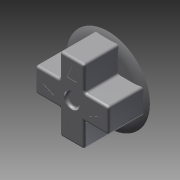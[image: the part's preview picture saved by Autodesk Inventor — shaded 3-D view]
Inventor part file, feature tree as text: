
AUTODESK INVENTOR PART (.ipt)
format: ipt  version: 2012 SP1 (Build 160190100, 190)  size: 237,056 bytes
history: native  units: in
note: dims shown in document units (in); Inventor stores cm internally (conversion verified against a paired STEP export)
features: extrude x4, fillet x4, sketch x4
ambient origin geometry x8: Origin, YZ Plane, XZ Plane, XY Plane, X Axis, Y Axis, Z Axis, Center Point
bodies: Solid1 (feature_tree)
feature tree (12):
  extrude  "Extrusion1"  Depth=0.22in
  extrude  "Extrusion2"  Depth=0.14in
  fillet  "Fillet1"  Radius=0.025in
  fillet  "Fillet2"  Radius=0.02in
  fillet  "Fillet3"  Radius=0.02in
  extrude  "Extrusion3"  Depth=0.26in
  extrude  "Extrusion4"  Depth=0.1in
  fillet  "Fillet4"  Radius=0.045in
  sketch  "Sketch1"  dims[d1=0.11in d2=0.22in]
  sketch  "Sketch2"  dims[d4=0.3in d5=0.0in d7=0.14in d8=0.025in d9=0.0in d10=0.02in d11=0.02in]
  sketch  "Sketch3"  dims[d12=0.02in d13=0.26in]
  sketch  "Sketch4"  dims[d14=0.26in d15=0.1in d16=0.045in d17=0.045in d18=0.1in d19=0.045in d20=0.045in d21=0.0025in d22=0.0in d23=0.025in d24=0.0in d25=0.25in]
